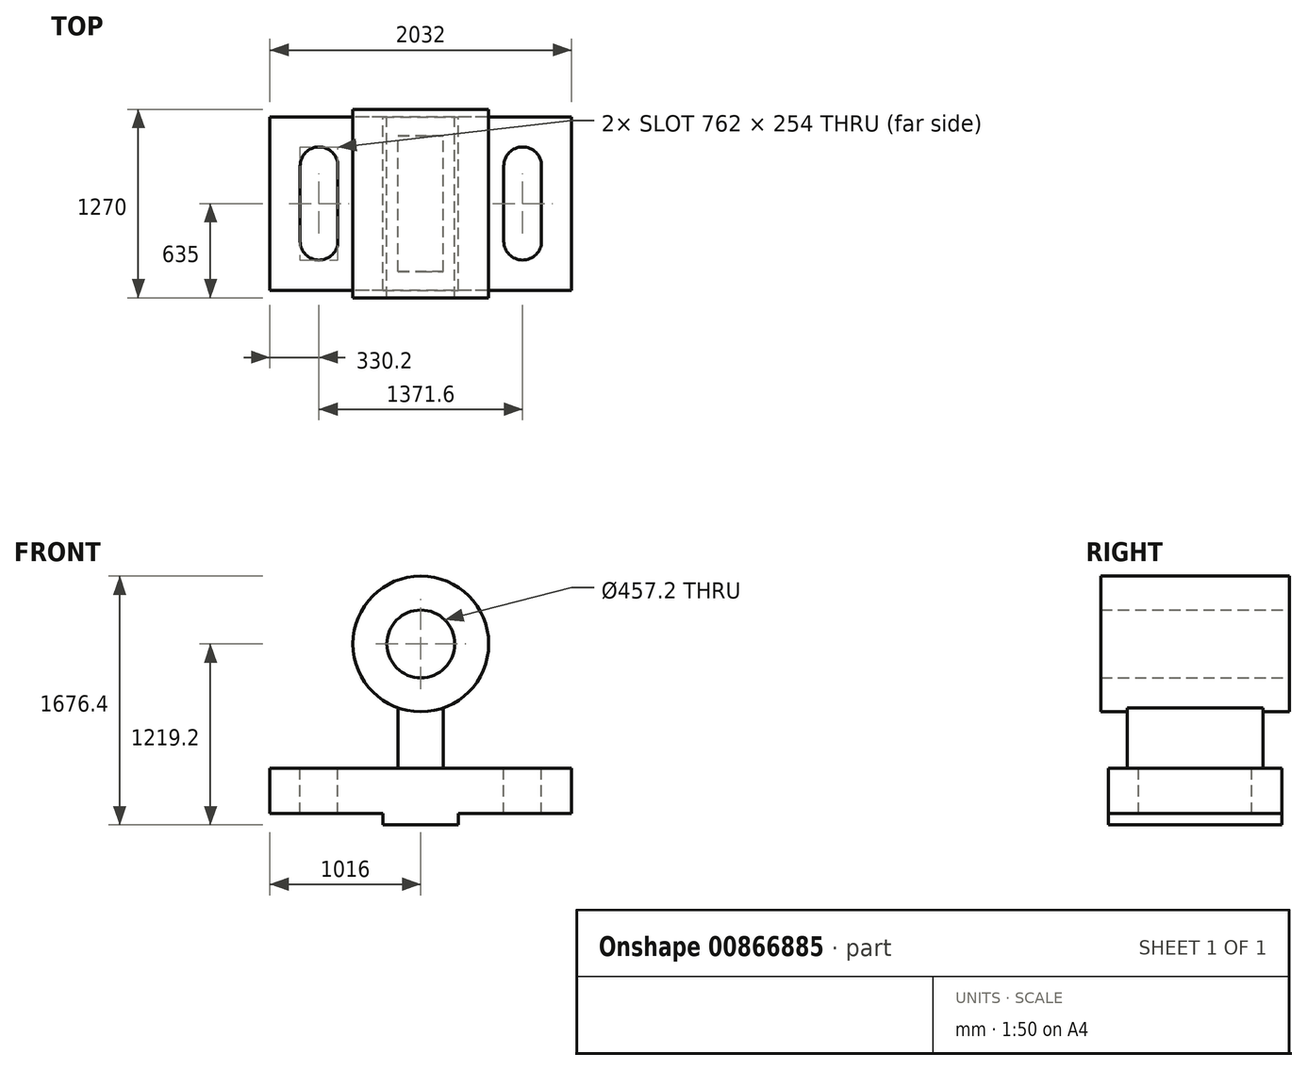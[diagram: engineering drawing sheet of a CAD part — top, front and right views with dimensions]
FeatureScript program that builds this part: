
annotation { "Feature Type Name" : "Feature", "Feature Type Description" : "" }
export const myFeature = defineFeature(function(context is Context, id is Id, definition is map)
    precondition{}
    {
        {
            var Q0;
            Q0=qCreatedBy(makeId("Front.planeOp"),FACE);
            var sketch = newSketch(context, id + "F0", { "sketchPlane" : qUnion([Q0])});
            skLineSegment(sketch, "E0.bottom", {"start": v(1016, 152.4) * mm, "end": v(-1016, 152.4) * mm});
            skLineSegment(sketch, "E0.top", {"start": v(1016, -152.4) * mm, "end": v(-1016, -152.4) * mm});
            skLineSegment(sketch, "E0.left", {"start": v(1016, 152.4) * mm, "end": v(1016, -152.4) * mm});
            skLineSegment(sketch, "E0.right", {"start": v(-1016, 152.4) * mm, "end": v(-1016, -152.4) * mm});
            skPoint(sketch, "E0.middle", {"position": v(0, 0) * mm});
            skLineSegment(sketch, "E1.bottom", {"start": v(-254, -152.4) * mm, "end": v(254, -152.4) * mm});
            skLineSegment(sketch, "E1.top", {"start": v(-254, -228.6) * mm, "end": v(254, -228.6) * mm});
            skLineSegment(sketch, "E1.left", {"start": v(-254, -152.4) * mm, "end": v(-254, -228.6) * mm});
            skLineSegment(sketch, "E1.right", {"start": v(254, -152.4) * mm, "end": v(254, -228.6) * mm});
            skLineSegment(sketch, "E2", {"start": v(0, -152.4) * mm, "end": v(0, 990.6) * mm});
            skCircle(sketch, "E3", {"center": v(0, 990.6) * mm, "radius": 228.6 * mm});
            skCircle(sketch, "E4", {"center": v(0, 990.6) * mm, "radius": 457.2 * mm});
            skLineSegment(sketch, "E5.bottom", {"start": v(152.4, 152.4) * mm, "end": v(-152.4, 152.4) * mm});
            skLineSegment(sketch, "E5.top", {"start": v(152.4, 685.8) * mm, "end": v(-152.4, 685.8) * mm});
            skLineSegment(sketch, "E5.left", {"start": v(152.4, 152.4) * mm, "end": v(152.4, 685.8) * mm});
            skLineSegment(sketch, "E5.right", {"start": v(-152.4, 152.4) * mm, "end": v(-152.4, 685.8) * mm});
            skPoint(sketch, "E5.middle", {"position": v(0, 419.1) * mm});
            skSolve(sketch);
        }
        {
            var Q0;
            {var subQ0=sQuery(id+"F0.wireOp",EDGE,"E0.right");Q0=makeQuery(id+"F0.imprint","IMPRINT",FACE,{"disambiguationData":[TD([[makeQuery(id+"F0.imprint","IMPRINT",EDGE,{"derivedFrom":subQ0}),1.0]])]});}
            var Q1;
            {var subQ0=sQuery(id+"F0.wireOp",EDGE,"E0.left");Q1=makeQuery(id+"F0.imprint","IMPRINT",FACE,{"disambiguationData":[TD([[makeQuery(id+"F0.imprint","IMPRINT",EDGE,{"derivedFrom":subQ0}),-1.0]])]});}
            var Q2;
            Q2=makeQuery(id+"F0.imprint","IMPRINT",FACE,{"disambiguationData":[TD([[makeQuery(id+"F0.imprint","IMPRINT",EDGE,{"derivedFrom":sQuery(id+"F0.wireOp",EDGE,"E1.top")}),1.0]])]});
            extrude(context, id + "F1", {"entities" : qUnion([Q0, Q1, Q2]), "endBound" : BoundingType.SYMMETRIC, "depth" : 1168.4 * mm, "offsetDistance" : 25.4 * mm});
        }
        {
            var Q0;
            {var subQ0=sQuery(id+"F0.wireOp",EDGE,"E5.bottom");var subQ1=sQuery(id+"F0.wireOp",EDGE,"E2");var subQ2=makeQuery(id+"F0.imprint","INTERSECT",VERTEX,{"derivedFrom":[subQ1,subQ0]});Q0=makeQuery(id+"F0.imprint","IMPRINT",FACE,{"disambiguationData":[TD([[makeQuery(id+"F0.imprint","IMPRINT",EDGE,{"disambiguationData":[TD([[subQ2,-1.0]])],"derivedFrom":subQ1}),1.0]])]});}
            var Q1;
            {var subQ0=sQuery(id+"F0.wireOp",EDGE,"E5.bottom");var subQ1=sQuery(id+"F0.wireOp",EDGE,"E2");var subQ2=makeQuery(id+"F0.imprint","INTERSECT",VERTEX,{"derivedFrom":[subQ1,subQ0]});Q1=makeQuery(id+"F0.imprint","IMPRINT",FACE,{"disambiguationData":[TD([[makeQuery(id+"F0.imprint","IMPRINT",EDGE,{"disambiguationData":[TD([[subQ2,-1.0]])],"derivedFrom":subQ1}),-1.0]])]});}
            extrude(context, id + "F2", {"entities" : qUnion([Q0, Q1]), "operationType" : NewBodyOperationType.ADD, "endBound" : BoundingType.SYMMETRIC, "depth" : 914.4 * mm, "offsetDistance" : 25.4 * mm});
        }
        {
            var Q0;
            Q0=makeQuery(id+"F0.imprint","IMPRINT",FACE,{"disambiguationData":[TD([[makeQuery(id+"F0.imprint","IMPRINT",EDGE,{"derivedFrom":sQuery(id+"F0.wireOp",EDGE,"E3")}),-1.0]])]});
            var Q1;
            {var subQ0=sQuery(id+"F0.wireOp",EDGE,"E5.top");var subQ1=sQuery(id+"F0.wireOp",EDGE,"E2");var subQ2=makeQuery(id+"F0.imprint","INTERSECT",VERTEX,{"derivedFrom":[subQ1,subQ0]});Q1=makeQuery(id+"F0.imprint","IMPRINT",FACE,{"disambiguationData":[TD([[makeQuery(id+"F0.imprint","IMPRINT",EDGE,{"disambiguationData":[TD([[subQ2,1.0]])],"derivedFrom":subQ1}),1.0]])]});}
            var Q2;
            {var subQ0=sQuery(id+"F0.wireOp",EDGE,"E5.top");var subQ1=sQuery(id+"F0.wireOp",EDGE,"E2");var subQ2=makeQuery(id+"F0.imprint","INTERSECT",VERTEX,{"derivedFrom":[subQ1,subQ0]});Q2=makeQuery(id+"F0.imprint","IMPRINT",FACE,{"disambiguationData":[TD([[makeQuery(id+"F0.imprint","IMPRINT",EDGE,{"disambiguationData":[TD([[subQ2,1.0]])],"derivedFrom":subQ1}),-1.0]])]});}
            extrude(context, id + "F3", {"entities" : qUnion([Q0, Q1, Q2]), "operationType" : NewBodyOperationType.ADD, "endBound" : BoundingType.SYMMETRIC, "depth" : 1270 * mm, "offsetDistance" : 25.4 * mm});
        }
        {
            var Q0;
            Q0=makeQuery(id+"F1.opExtrude","SWEPT_FACE",FACE,{"disambiguationData":[OSD([sQuery(id+"F0.wireOp",EDGE,"E0.bottom"),sQuery(id+"F0.wireOp",EDGE,"E5.bottom")])]});
            var sketch = newSketch(context, id + "F4", { "sketchPlane" : qUnion([Q0])});
            skLineSegment(sketch, "E6", {"start": v(-1016, 0) * mm, "end": v(-685.8, 0) * mm});
            skLineSegment(sketch, "E7", {"start": v(1016, 0) * mm, "end": v(685.8, 0) * mm});
            skLineSegment(sketch, "E8.bottom", {"start": v(-558.8, -254) * mm, "end": v(-812.8, -254) * mm});
            skLineSegment(sketch, "E8.top", {"start": v(-558.8, 254) * mm, "end": v(-812.8, 254) * mm});
            skLineSegment(sketch, "E8.left", {"start": v(-558.8, -254) * mm, "end": v(-558.8, 254) * mm});
            skLineSegment(sketch, "E8.right", {"start": v(-812.8, -254) * mm, "end": v(-812.8, 254) * mm});
            skPoint(sketch, "E8.middle", {"position": v(-685.8, 0) * mm});
            skArc(sketch, "E9", {"start": v(-558.8, 254) * mm, "mid": v(-685.8, 381) * mm, "end": v(-812.8, 254) * mm});
            skArc(sketch, "E10", {"start": v(-558.8, -254) * mm, "mid": v(-685.8, -381) * mm, "end": v(-812.8, -254) * mm});
            skLineSegment(sketch, "E11.bottom", {"start": v(812.8, -254) * mm, "end": v(558.8, -254) * mm});
            skLineSegment(sketch, "E11.top", {"start": v(812.8, 254) * mm, "end": v(558.8, 254) * mm});
            skLineSegment(sketch, "E11.left", {"start": v(812.8, -254) * mm, "end": v(812.8, 254) * mm});
            skLineSegment(sketch, "E11.right", {"start": v(558.8, -254) * mm, "end": v(558.8, 254) * mm});
            skPoint(sketch, "E11.middle", {"position": v(685.8, 0) * mm});
            skArc(sketch, "E12", {"start": v(812.8, -254) * mm, "mid": v(685.8, -381) * mm, "end": v(558.8, -254) * mm});
            skArc(sketch, "E13", {"start": v(812.8, 254) * mm, "mid": v(685.8, 381) * mm, "end": v(558.8, 254) * mm});
            skSolve(sketch);
        }
        {
            var Q0;
            {var subQ1=sQuery(id+"F4.wireOp",EDGE,"E8.bottom");Q0=makeQuery(id+"F4.imprint","IMPRINT",FACE,{"disambiguationData":[TD([[makeQuery(id+"F4.imprint","IMPRINT",EDGE,{"derivedFrom":subQ1}),-1.0]])]});}
            var Q1;
            Q1=makeQuery(id+"F4.imprint","IMPRINT",FACE,{"disambiguationData":[TD([[makeQuery(id+"F4.imprint","IMPRINT",EDGE,{"derivedFrom":sQuery(id+"F4.wireOp",EDGE,"E8.top")}),-1.0]])]});
            var Q2;
            Q2=makeQuery(id+"F4.imprint","IMPRINT",FACE,{"disambiguationData":[TD([[makeQuery(id+"F4.imprint","IMPRINT",EDGE,{"derivedFrom":sQuery(id+"F4.wireOp",EDGE,"E8.bottom")}),1.0]])]});
            var Q3;
            {var subQ3=sQuery(id+"F4.wireOp",EDGE,"E11.bottom");Q3=makeQuery(id+"F4.imprint","IMPRINT",FACE,{"disambiguationData":[TD([[makeQuery(id+"F4.imprint","IMPRINT",EDGE,{"derivedFrom":subQ3}),-1.0]])]});}
            var Q4;
            Q4=makeQuery(id+"F4.imprint","IMPRINT",FACE,{"disambiguationData":[TD([[makeQuery(id+"F4.imprint","IMPRINT",EDGE,{"derivedFrom":sQuery(id+"F4.wireOp",EDGE,"E11.top")}),-1.0]])]});
            var Q5;
            Q5=makeQuery(id+"F4.imprint","IMPRINT",FACE,{"disambiguationData":[TD([[makeQuery(id+"F4.imprint","IMPRINT",EDGE,{"derivedFrom":sQuery(id+"F4.wireOp",EDGE,"E11.bottom")}),1.0]])]});
            extrude(context, id + "F5", {"entities" : qUnion([Q0, Q1, Q2, Q3, Q4, Q5]), "operationType" : NewBodyOperationType.REMOVE, "endBound" : BoundingType.THROUGH_ALL, "oppositeDirection" : true, "depth" : 25.4 * mm, "offsetDistance" : 25.4 * mm});
        }
    });
